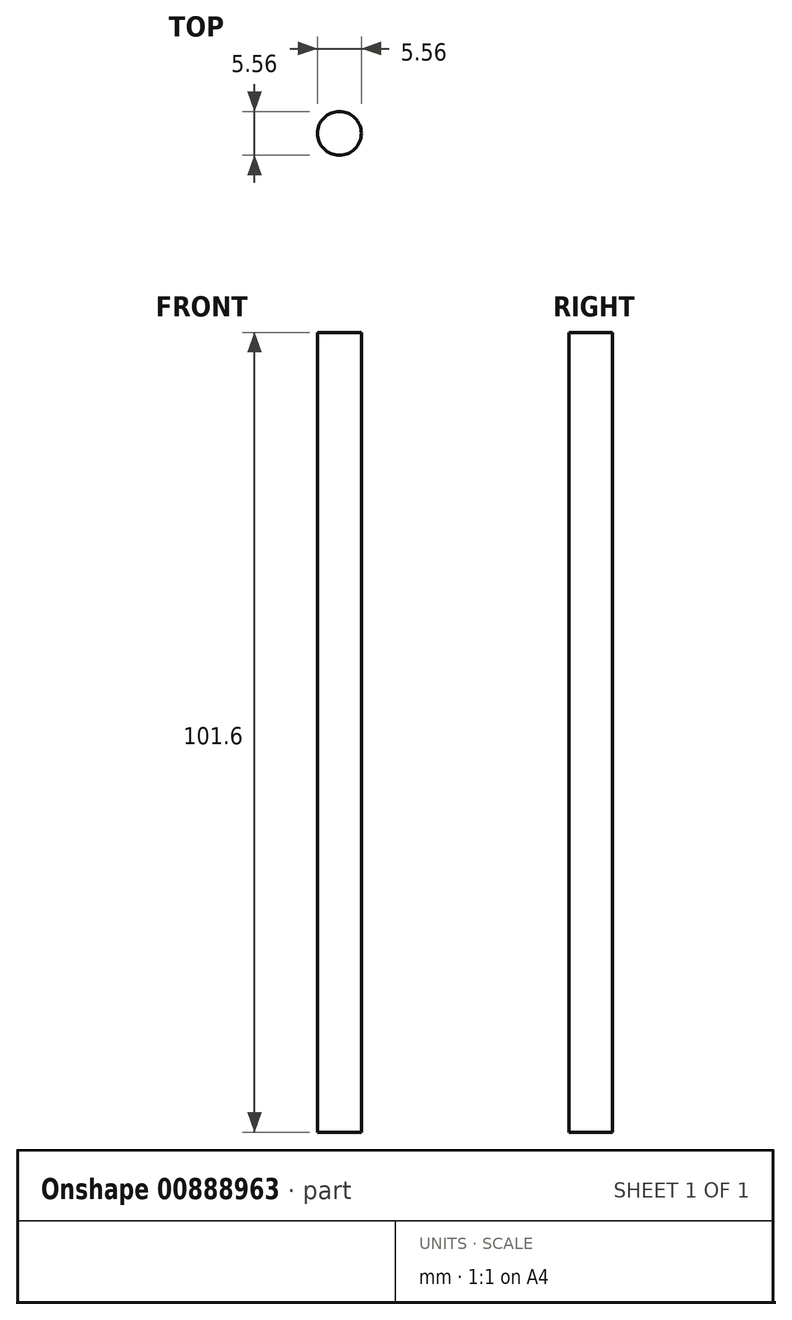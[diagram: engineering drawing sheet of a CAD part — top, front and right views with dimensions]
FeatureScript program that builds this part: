
annotation { "Feature Type Name" : "Feature", "Feature Type Description" : "" }
export const myFeature = defineFeature(function(context is Context, id is Id, definition is map)
    precondition{}
    {
        {
            var Q0;
            Q0=qCreatedBy(makeId("Top.planeOp"),FACE);
            var sketch = newSketch(context, id + "F0", { "sketchPlane" : qUnion([Q0])});
            skCircle(sketch, "E0", {"center": v(-60.82, 63.94) * mm, "radius": 2.78 * mm});
            skSolve(sketch);
        }
        {
            var Q0;
            Q0=makeQuery(id+"F0.imprint","IMPRINT",FACE,{"disambiguationData":[TD([[makeQuery(id+"F0.imprint","IMPRINT",EDGE,{"derivedFrom":sQuery(id+"F0.wireOp",EDGE,"E0")}),1.0]])]});
            extrude(context, id + "F1", {"entities" : qUnion([Q0]), "depth" : 101.6 * mm, "offsetDistance" : 25.4 * mm});
        }
    });
